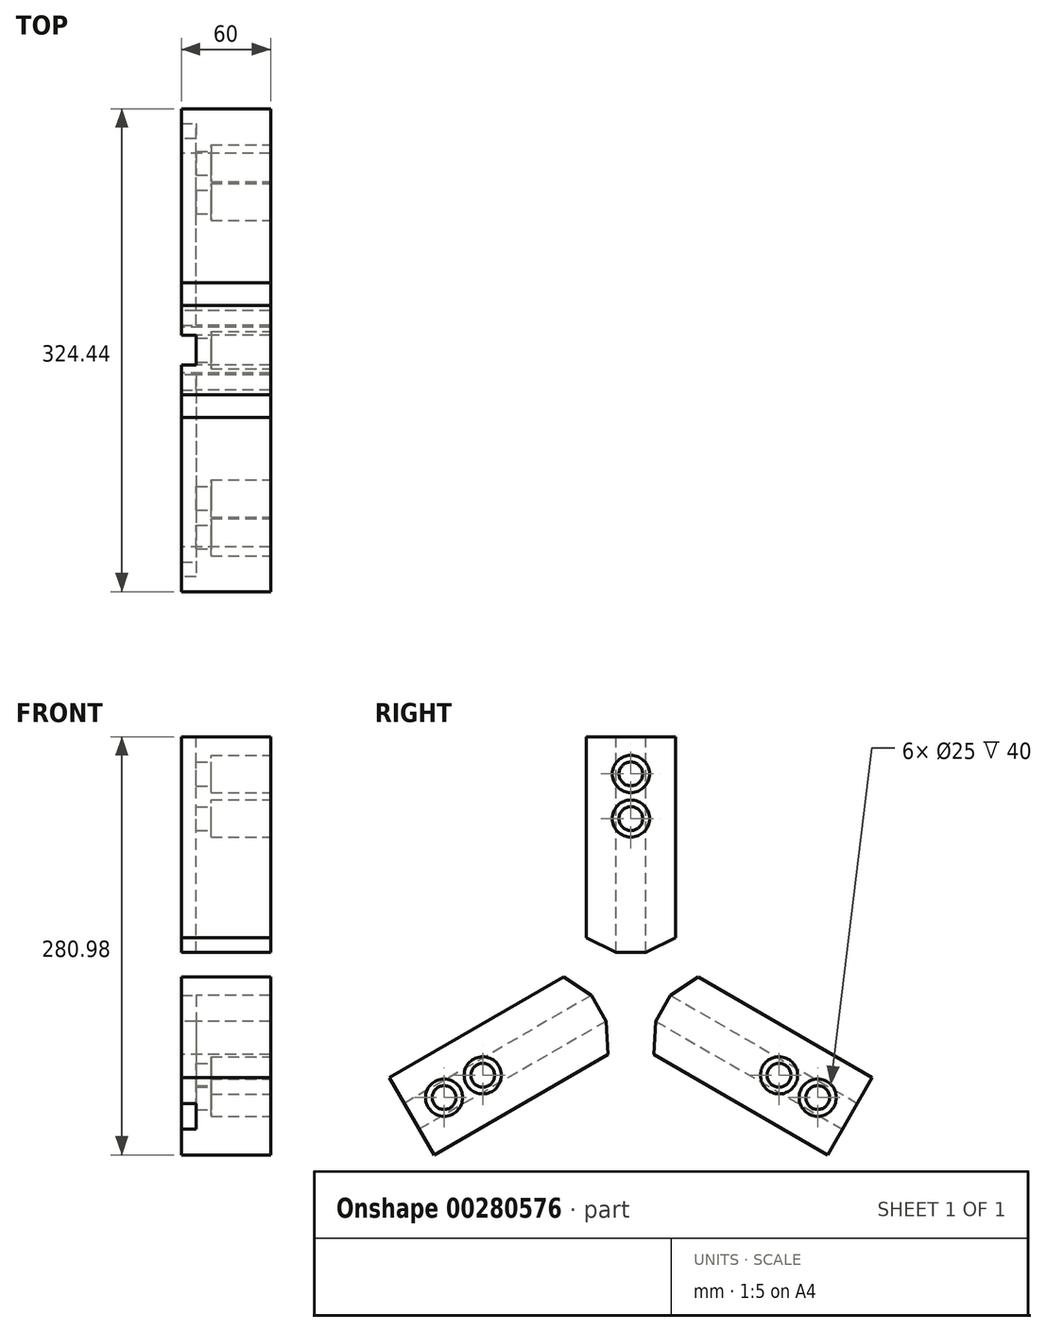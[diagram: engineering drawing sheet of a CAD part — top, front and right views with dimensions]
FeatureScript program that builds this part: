
annotation { "Feature Type Name" : "Feature", "Feature Type Description" : "" }
export const myFeature = defineFeature(function(context is Context, id is Id, definition is map)
    precondition{}
    {
        {
            var Q0;
            Q0=qCreatedBy(makeId("Right.planeOp"),FACE);
            var sketch = newSketch(context, id + "F0", { "sketchPlane" : qUnion([Q0])});
            skCircle(sketch, "E0", {"center": v(0, 0) * mm, "radius": 25 * mm});
            skLineSegment(sketch, "E1", {"start": v(0, 198.34) * mm, "end": v(0, 25) * mm, "construction": true});
            skLineSegment(sketch, "E2", {"start": v(0, 25) * mm, "end": v(0, -30.8) * mm, "construction": true});
            skLineSegment(sketch, "E3", {"start": v(0, 25) * mm, "end": v(10, 25) * mm});
            skLineSegment(sketch, "E4", {"start": v(10, 25) * mm, "end": v(30, 35) * mm});
            skLineSegment(sketch, "E5", {"start": v(30, 35) * mm, "end": v(30, 170) * mm});
            skLineSegment(sketch, "E6", {"start": v(30, 170) * mm, "end": v(0, 170) * mm});
            skLineSegment(sketch, "E7", {"start": v(0, 170) * mm, "end": v(-30, 170) * mm});
            skLineSegment(sketch, "E8", {"start": v(-30, 170) * mm, "end": v(-30, 35) * mm});
            skLineSegment(sketch, "E9", {"start": v(-30, 35) * mm, "end": v(-10, 25) * mm});
            skLineSegment(sketch, "E10", {"start": v(-10, 25) * mm, "end": v(0, 25) * mm});
            skSolve(sketch);
        }
        {
            var Q0;
            Q0=makeQuery(id+"F0.imprint","IMPRINT",FACE,{"disambiguationData":[TD([[makeQuery(id+"F0.imprint","IMPRINT",EDGE,{"derivedFrom":sQuery(id+"F0.wireOp",EDGE,"E3")}),1.0]])]});
            extrude(context, id + "F1", {"entities" : qUnion([Q0]), "depth" : 60 * mm});
        }
        {
            var Q0;
            Q0=makeQuery(id+"F1.opExtrude","CAP_FACE",FACE,{"disambiguationData":[OSD([sQuery(id+"F0.wireOp",EDGE,"E3"),sQuery(id+"F0.wireOp",EDGE,"E4"),sQuery(id+"F0.wireOp",EDGE,"E5"),sQuery(id+"F0.wireOp",EDGE,"E6"),sQuery(id+"F0.wireOp",EDGE,"E7"),sQuery(id+"F0.wireOp",EDGE,"E8"),sQuery(id+"F0.wireOp",EDGE,"E9"),sQuery(id+"F0.wireOp",EDGE,"E10")])],"isStart":false});
            var sketch = newSketch(context, id + "F2", { "sketchPlane" : qUnion([Q0])});
            skCircle(sketch, "E11", {"center": v(0, 145) * mm, "radius": 8 * mm});
            skCircle(sketch, "E12", {"center": v(0, 115) * mm, "radius": 8 * mm});
            skCircle(sketch, "E13", {"center": v(0, 145) * mm, "radius": 12.5 * mm});
            skCircle(sketch, "E14", {"center": v(0, 115) * mm, "radius": 12.5 * mm});
            skSolve(sketch);
        }
        {
            var Q0;
            Q0=makeQuery(id+"F2.imprint","IMPRINT",FACE,{"disambiguationData":[TD([[makeQuery(id+"F2.imprint","IMPRINT",EDGE,{"derivedFrom":sQuery(id+"F2.wireOp",EDGE,"E11")}),1.0]])]});
            var Q1;
            Q1=makeQuery(id+"F2.imprint","IMPRINT",FACE,{"disambiguationData":[TD([[makeQuery(id+"F2.imprint","IMPRINT",EDGE,{"derivedFrom":sQuery(id+"F2.wireOp",EDGE,"E12")}),1.0]])]});
            extrude(context, id + "F3", {"entities" : qUnion([Q0, Q1]), "operationType" : NewBodyOperationType.REMOVE, "endBound" : BoundingType.UP_TO_NEXT, "oppositeDirection" : true, "depth" : 25 * mm});
        }
        {
            var Q0;
            Q0=qSketchRegion(id+"F2",true);
            extrude(context, id + "F4", {"entities" : qUnion([Q0]), "operationType" : NewBodyOperationType.REMOVE, "oppositeDirection" : true, "depth" : 40 * mm});
        }
        {
            var Q0;
            Q0=makeQuery(id+"F1.opExtrude","SWEPT_FACE",FACE,{"disambiguationData":[OSD([sQuery(id+"F0.wireOp",EDGE,"E6"),sQuery(id+"F0.wireOp",EDGE,"E7")])]});
            var sketch = newSketch(context, id + "F5", { "sketchPlane" : qUnion([Q0])});
            skLineSegment(sketch, "E15", {"start": v(0, 0) * mm, "end": v(0, -10) * mm});
            skLineSegment(sketch, "E16", {"start": v(0, -10) * mm, "end": v(10, -10) * mm});
            skLineSegment(sketch, "E17", {"start": v(10, -10) * mm, "end": v(10, 0) * mm});
            skLineSegment(sketch, "E18", {"start": v(10, 0) * mm, "end": v(10, 10) * mm});
            skLineSegment(sketch, "E19", {"start": v(10, 10) * mm, "end": v(0, 10) * mm});
            skLineSegment(sketch, "E20", {"start": v(0, 10) * mm, "end": v(0, 0) * mm});
            skSolve(sketch);
        }
        {
            var Q0;
            Q0=qSketchRegion(id+"F5",true);
            var Q1;
            Q1=makeQuery(id+"F1.opExtrude","SWEPT_FACE",FACE,{"disambiguationData":[OSD([sQuery(id+"F0.wireOp",EDGE,"E3"),sQuery(id+"F0.wireOp",EDGE,"E10")])]});
            extrude(context, id + "F6", {"entities" : qUnion([Q0]), "operationType" : NewBodyOperationType.REMOVE, "endBound" : BoundingType.UP_TO_SURFACE, "oppositeDirection" : true, "endBoundEntityFace" : qUnion([Q1]), "depth" : 25 * mm});
        }
        {
            var Q0;
            Q0=qCreatedBy(makeId("Front.planeOp"),FACE);
            var sketch = newSketch(context, id + "F7", { "sketchPlane" : qUnion([Q0])});
            skLineSegment(sketch, "E21", {"start": v(0, 0) * mm, "end": v(73.98, 0) * mm, "construction": true});
            skSolve(sketch);
        }
        {
            var Q0;
            Q0=makeQuery(id+"F1.opExtrude","SWEPT_BODY",BODY,{"disambiguationData":[OSD([sQuery(id+"F0.wireOp",EDGE,"E3"),sQuery(id+"F0.wireOp",EDGE,"E4"),sQuery(id+"F0.wireOp",EDGE,"E5"),sQuery(id+"F0.wireOp",EDGE,"E6"),sQuery(id+"F0.wireOp",EDGE,"E7"),sQuery(id+"F0.wireOp",EDGE,"E8"),sQuery(id+"F0.wireOp",EDGE,"E9"),sQuery(id+"F0.wireOp",EDGE,"E10")])]});
            var Q1;
            Q1=sQuery(id+"F7.wireOp",EDGE,"E21");
            circularPattern(context, id + "F8", {"entities" : qUnion([Q0]), "axis" : qUnion([Q1]), "angle" : 360 * degree, "instanceCount" : 3, "equalSpace" : true, "computeTransformsWithoutBuiltin" : true});
        }
        {
            var Q0;
            Q0=makeQuery(id+"F1.opExtrude","SWEPT_BODY",BODY,{"disambiguationData":[OSD([sQuery(id+"F0.wireOp",EDGE,"E3"),sQuery(id+"F0.wireOp",EDGE,"E4"),sQuery(id+"F0.wireOp",EDGE,"E5"),sQuery(id+"F0.wireOp",EDGE,"E6"),sQuery(id+"F0.wireOp",EDGE,"E7"),sQuery(id+"F0.wireOp",EDGE,"E8"),sQuery(id+"F0.wireOp",EDGE,"E9"),sQuery(id+"F0.wireOp",EDGE,"E10")])]});
            var Q1;
            Q1=makeQuery(id+"F8.opPattern","COPY",BODY,{"derivedFrom":makeQuery(id+"F1.opExtrude","SWEPT_BODY",BODY,{"disambiguationData":[OSD([sQuery(id+"F0.wireOp",EDGE,"E3"),sQuery(id+"F0.wireOp",EDGE,"E4"),sQuery(id+"F0.wireOp",EDGE,"E5"),sQuery(id+"F0.wireOp",EDGE,"E6"),sQuery(id+"F0.wireOp",EDGE,"E7"),sQuery(id+"F0.wireOp",EDGE,"E8"),sQuery(id+"F0.wireOp",EDGE,"E9"),sQuery(id+"F0.wireOp",EDGE,"E10")])]}),"instanceName":"1"});
            var Q2;
            Q2=makeQuery(id+"F8.opPattern","COPY",BODY,{"derivedFrom":makeQuery(id+"F1.opExtrude","SWEPT_BODY",BODY,{"disambiguationData":[OSD([sQuery(id+"F0.wireOp",EDGE,"E3"),sQuery(id+"F0.wireOp",EDGE,"E4"),sQuery(id+"F0.wireOp",EDGE,"E5"),sQuery(id+"F0.wireOp",EDGE,"E6"),sQuery(id+"F0.wireOp",EDGE,"E7"),sQuery(id+"F0.wireOp",EDGE,"E8"),sQuery(id+"F0.wireOp",EDGE,"E9"),sQuery(id+"F0.wireOp",EDGE,"E10")])]}),"instanceName":"2"});
            transform(context, id + "F9", {"entities" : qUnion([Q0, Q1, Q2]), "transformType" : TransformType.TRANSLATION_3D, "dx" : 3 * mm, "dy" : 0 * mm, "dz" : 0 * mm, "makeCopy" : false});
        }
    });
